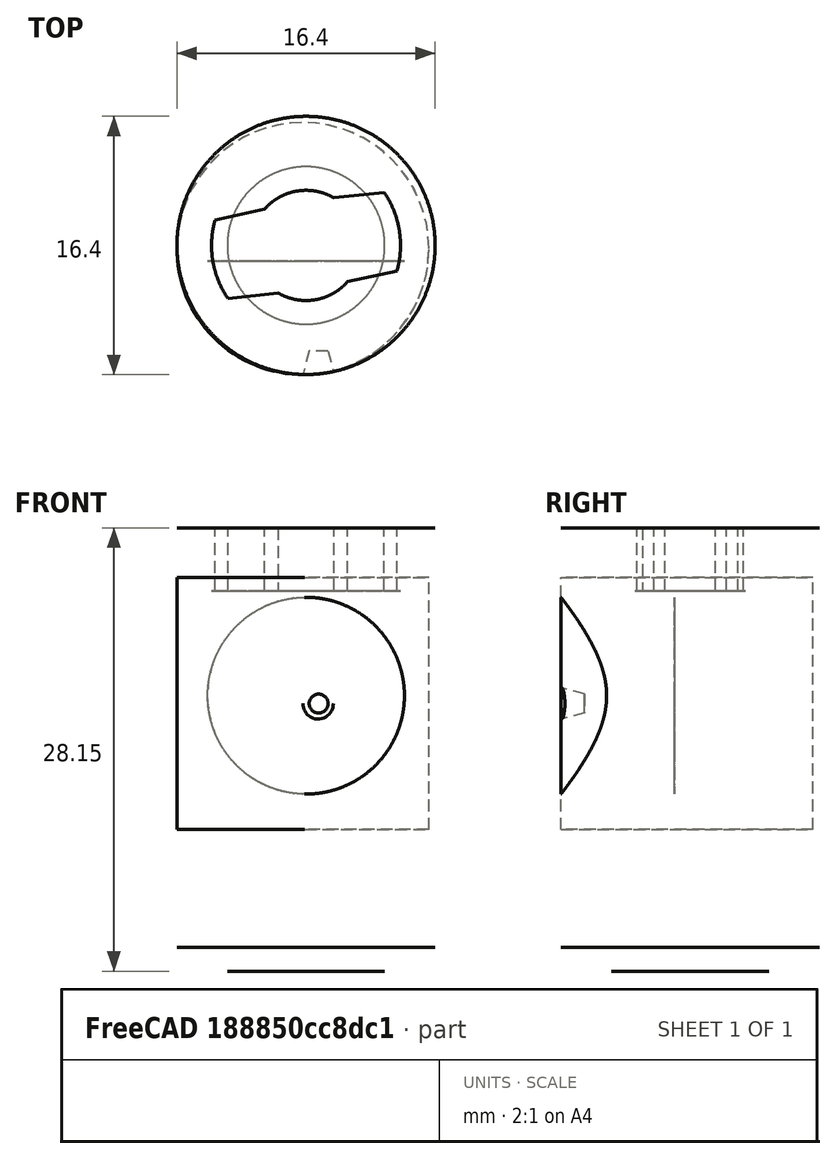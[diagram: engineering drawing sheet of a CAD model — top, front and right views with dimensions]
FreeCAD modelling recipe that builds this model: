
FCSTD DOCUMENT  (FreeCAD 0.19R24267 +148 (Git))
Label: rotating feeder modified
License: All rights reserved
LicenseURL: http://en.wikipedia.org/wiki/All_rights_reserved
objects: PartDesign::FeatureBase×2, PartDesign::Body×2, Part::Feature×1, Part::Cylinder×1, Part::Cone×1, Part::Cut×1, Part::Compound×1
note: 9 computed .brp shape members not serialized (recipe doc carries the construction recipe); baked Part::Feature solids carry a one-line shape summary decoded from their .brp

FEATURE [Part::Feature] _________________4001_solid  label="_________________4001 (Solid)"
  shape: bbox 16.4 x 16.4 x 28.15 mm, 12032 faces (baked)
FEATURE [Part::Cylinder] Cylinder
  Angle = 360
  AttacherType = Attacher::AttachEngine3D
  Height = 16
  Placement = pos=(8,8.5,11) rot=(0,0,1;0rad)
  Radius = 8
FEATURE [PartDesign::FeatureBase] BaseFeature
  BaseFeature = -> _________________4001_solid
FEATURE [PartDesign::Body] Body
  BaseFeature = -> _________________4001_solid
  Group = -> [BaseFeature]
  Origin = -> Origin
  Tip = -> BaseFeature
FEATURE [PartDesign::FeatureBase] BaseFeature001
  BaseFeature = -> Cylinder
FEATURE [PartDesign::Body] Body001
  BaseFeature = -> Cylinder
  Group = -> [BaseFeature001]
  Origin = -> Origin001
  Tip = -> BaseFeature001
FEATURE [Part::Cone] Cone
  Angle = 360
  AttacherType = Attacher::AttachEngine3D
  Height = 1.5
  Placement = pos=(1,-6.5,8) rot=(1,0,0;1.5708rad)
  Radius1 = 0.6
  Radius2 = 1
FEATURE [Part::Cut] Cut
  Base = -> Body001
  Placement = pos=(8,8,9) rot=(0,0,1;0rad)
  Tool = -> Cone
FEATURE [Part::Compound] Compound
  Links = -> [Body,Cut]
